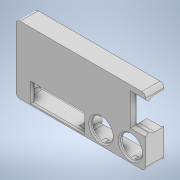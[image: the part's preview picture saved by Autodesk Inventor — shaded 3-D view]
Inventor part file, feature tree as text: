
AUTODESK INVENTOR PART (.ipt)
format: ipt  version: 2021 (Build 250183000, 183)  size: 570,880 bytes
history: native  units: mm
features: sketch x27, extrude x24, fillet x8, chamfer x7, hole x3
ambient origin geometry x8: Origin, YZ Plane, XZ Plane, XY Plane, X Axis, Y Axis, Z Axis, Center Point
bodies: Solid1 (feature_tree)
feature tree (69):
  extrude  "Extrusion1"  Depth=52.0mm
  extrude  "Extrusion2"  Depth=50.0mm
  extrude  "Extrusion3"  Depth=2.0mm
  extrude  "Extrusion4"  Depth=2.0mm
  fillet  "Fillet1"  Radius=2.0mm
  chamfer  "Chamfer1"  Distance=12.0mm
  extrude  "Extrusion5"  Depth=10.4mm
  extrude  "Extrusion6"  Depth=10.4mm
  extrude  "Extrusion7"  Depth=17.0mm
  extrude  "Extrusion8"  Depth=2.0mm
  extrude  "Extrusion9"  Depth=2.0mm
  chamfer  "Chamfer2"  Distance=2.0mm
  extrude  "Extrusion10"  Depth=2.0mm TaperAngle=45.0deg
  fillet  "Fillet3"  Radius=88.0mm
  chamfer  "Chamfer3"  Distance=20.0mm
  extrude  "Extrusion11"  Depth=2.0mm TaperAngle=0.0deg
  extrude  "Extrusion12"  Depth=11.0mm
  hole  "Hole1"  [1 undecoded]
  extrude  "Extrusion13"  TaperAngle=0.0deg  [1 undecoded]
  hole  "Hole2"  [1 undecoded]
  extrude  "Extrusion14"  Depth=2.0mm
  extrude  "Extrusion15"  Depth=2.0mm TaperAngle=45.0deg
  extrude  "Extrusion16"  Depth=40.0mm
  extrude  "Extrusion17"  Depth=6.0mm
  extrude  "Extrusion22"  Depth=16.0mm
  extrude  "Extrusion23"  Depth=2.0mm
  extrude  "Extrusion24"  Depth=2.0mm
  chamfer  "Chamfer8"  Distance=49.0mm
  chamfer  "Chamfer9"  Distance=85.0mm
  fillet  "Fillet5"  Radius=49.0mm
  extrude  "Extrusion25"  Depth=2.0mm
  fillet  "Fillet6"  Radius=2.0mm
  chamfer  "Chamfer11"  Distance=2.0mm
  extrude  "Extrusion26"  Depth=2.0mm
  hole  "Hole3"  [1 undecoded]
  chamfer  "Chamfer12"  Distance=5.0mm
  fillet  "Fillet7"  Radius=12.0mm
  extrude  "Extrusion29"  Depth=2.0mm
  extrude  "Extrusion31"  Depth=2.0mm
  fillet  "Fillet10"  Radius=2.0mm
  fillet  "Fillet11"  Radius=5.0mm
  fillet  "Fillet12"  Radius=12.0mm
  sketch  "Sketch1"  dims[d0=100.0mm d1=52.0mm]
  sketch  "Sketch2"  dims[d2=26.0mm d3=50.0mm]
  sketch  "Sketch3"  dims[d4=2.0mm d5=0.0mm d6=2.0mm]
  sketch  "Sketch4"  dims[d7=2.0mm d8=2.0mm d9=2.0mm d10=12.0mm d11=0.0mm]
  sketch  "Sketch5"  dims[d12=65.5mm d13=10.4mm]
  sketch  "Sketch6"  dims[d14=88.25mm d15=10.4mm]
  sketch  "Sketch7"  dims[d16=17.0mm d17=17.0mm]
  sketch  "Sketch8"  dims[d18=2.0mm d19=0.0mm d20=40.0mm]
  sketch  "Sketch9"  dims[d21=13.0mm d22=2.0mm]
  sketch  "Sketch10"  dims[d23=12.0mm d24=2.0mm d25=0.0mm]
  sketch  "Sketch11"  dims[d26=3.0mm d27=1.0mm d28=2.0mm d29=45.0deg d30=88.0mm]
  sketch  "Sketch12"  dims[d31=29.0mm]
  sketch  "Sketch13"  dims[d32=23.0mm d33=20.0mm d34=0.0mm]
  sketch  "Sketch14"  dims[d35=2.0mm d36=0.0mm d37=2.0mm d38=0.0mm]
  sketch  "Sketch15"  dims[d39=11.0mm d40=11.0mm]
  sketch  "Sketch16"  dims[d41=42.0mm d42=29.0mm]
  sketch  "Sketch17"  dims[d43=7.0mm d44=0.0mm]
  sketch  "Sketch18"  dims[d45=5.8mm d46=5.8mm]
  sketch  "Sketch19"  dims[d47=2.0mm d48=0.0mm d49=12.0mm]
  sketch  "Sketch24"  dims[d50=20.0mm d51=0.0mm d52=2.0mm d53=2.0mm d54=45.0deg]
  sketch  "Sketch25"  dims[d56=30.0mm d57=40.0mm]
  sketch  "Sketch27"  dims[d58=3.5mm d59=6.0mm]
  sketch  "Sketch28"  dims[d60=14.0mm d61=16.0mm]
  sketch  "Sketch29"  dims[d62=2.0mm d63=0.0mm d64=1.0mm]
  sketch  "Sketch30"  dims[d65=1.0mm d66=2.0mm d67=45.0deg d68=3.0mm]
  sketch  "Sketch33"  dims[d69=49.0mm]
  sketch  "Sketch35"  dims[d70=60.0mm d71=49.0mm d72=85.0mm d73=49.0mm d74=2.0mm d75=2.0mm d76=2.0mm d77=5.0mm d78=5.0mm d79=5.0mm d80=12.0mm d81=0.0mm d82=3.0mm d83=3.0mm d84=2.0mm d85=5.0mm d86=12.0mm d87=0.0mm d88=2.0mm d89=6.0mm d90=4.0mm d91=2.0mm d92=90.0deg d93=6.5mm d94=20.594885mm d95=8.0mm d96=97.0mm d97=4.2mm d98=12.0mm d99=0.0mm d100=2.0mm d101=6.0mm d102=4.0mm d103=2.0mm d104=90.0deg d105=6.5mm d106=20.594885mm d107=7.0mm d108=5.8mm d109=5.8mm d110=2.0mm d111=11.0mm d112=0.0mm d113=1.0mm d114=0.0mm d115=2.0mm d116=10.0mm d117=0.0mm d118=0.0mm d119=1.0mm d120=0.0mm d169=7.0mm d170=14.0mm d171=0.0mm d172=12.0mm d173=10.0mm d174=0.0mm d182=4.0mm d183=0.0mm d184=0.0mm d185=10.0mm d186=0.0mm d187=2.0mm d188=2.0mm d189=45.0deg d190=2.0mm d191=2.0mm d192=45.0deg d193=3.0mm d194=17.0mm d195=17.0mm d196=5.0mm d197=0.0mm d201=2.0mm d202=1.5mm d203=2.0mm d204=45.0deg d205=50.0mm d206=3.0mm d207=5.0mm d208=7.5mm d209=0.0mm d210=2.0mm d211=6.0mm d212=4.0mm d213=2.0mm d214=90.0deg d215=6.5mm d216=20.594885mm d217=3.49mm d218=2.0mm d219=45.0deg d220=2.0mm d236=2.0mm d237=0.0mm d243=1.5mm d244=14.0mm d245=0.0mm d246=2.0mm d247=2.0mm d248=2.0mm d160=0.5mm d161=0.872665mm d162=0.5mm d163=0.872665mm d221=0.375mm]
note: 4 required parameter values undecoded (feature->parameter linkage not recoverable at this tier; creation-order binding heuristic only, values carry confidence <= 0.55)
